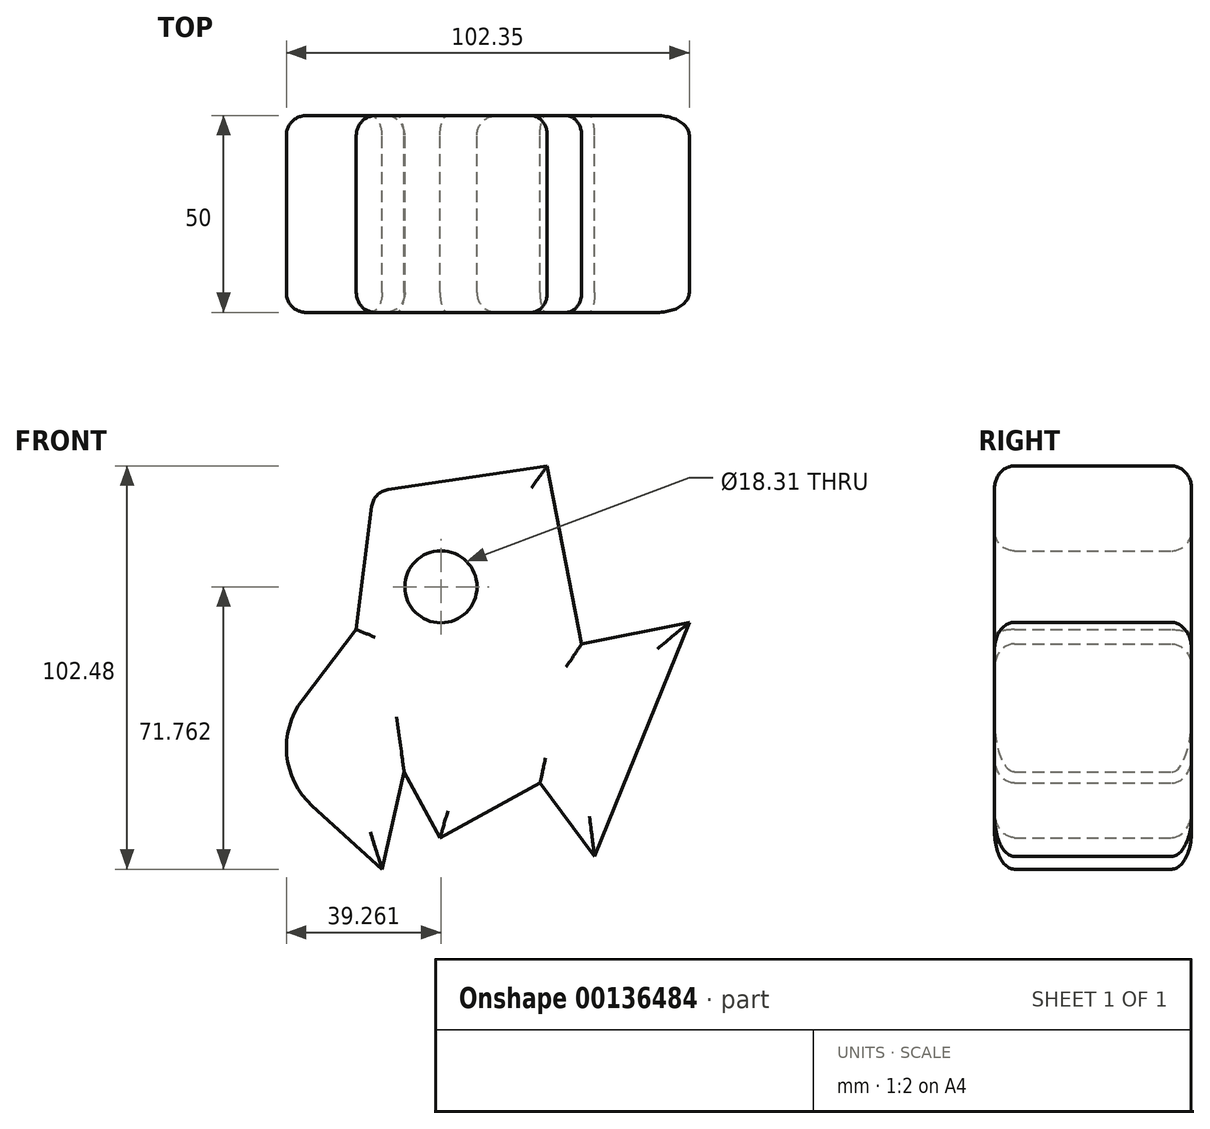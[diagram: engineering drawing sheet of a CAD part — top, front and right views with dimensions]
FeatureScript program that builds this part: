
annotation { "Feature Type Name" : "Feature", "Feature Type Description" : "" }
export const myFeature = defineFeature(function(context is Context, id is Id, definition is map)
    precondition{}
    {
        {
            var Q0;
            Q0=qCreatedBy(makeId("Front.planeOp"),FACE);
            var sketch = newSketch(context, id + "F0", { "sketchPlane" : qUnion([Q0])});
            skLineSegment(sketch, "E0", {"start": v(-30.63, 23.89) * mm, "end": v(-55.43, -8.57) * mm});
            skLineSegment(sketch, "E1", {"start": v(-55.43, -8.57) * mm, "end": v(-24.07, -37.02) * mm});
            skLineSegment(sketch, "E2", {"start": v(-9.35, -28.99) * mm, "end": v(16.05, -15.13) * mm});
            skLineSegment(sketch, "E3", {"start": v(16.05, -15.13) * mm, "end": v(29.9, -33.73) * mm});
            skLineSegment(sketch, "E4", {"start": v(29.9, -33.73) * mm, "end": v(53.97, 25.71) * mm});
            skLineSegment(sketch, "E5", {"start": v(53.97, 25.71) * mm, "end": v(26.62, 20.24) * mm});
            skLineSegment(sketch, "E6", {"start": v(26.62, 20.24) * mm, "end": v(17.87, 65.46) * mm});
            skLineSegment(sketch, "E7", {"start": v(17.87, 65.46) * mm, "end": v(-26.26, 58.9) * mm});
            skLineSegment(sketch, "E8", {"start": v(-26.26, 58.9) * mm, "end": v(-30.63, 23.89) * mm});
            skCircle(sketch, "E9", {"center": v(-9.12, 34.74) * mm, "radius": 9.16 * mm});
            skLineSegment(sketch, "E10", {"start": v(-18.47, -12.28) * mm, "end": v(-24.07, -37.02) * mm});
            skLineSegment(sketch, "E11", {"start": v(-18.47, -12.28) * mm, "end": v(-9.35, -28.99) * mm});
            skSolve(sketch);
        }
        {
            var Q0;
            Q0=makeQuery(id+"F0.imprint","IMPRINT",FACE,{"disambiguationData":[TD([[makeQuery(id+"F0.imprint","IMPRINT",EDGE,{"derivedFrom":sQuery(id+"F0.wireOp",EDGE,"E0")}),1.0]])]});
            extrude(context, id + "F1", {"entities" : qUnion([Q0]), "depth" : 50 * mm});
        }
        {
            var Q0;
            Q0=makeQuery(id+"F1.opExtrude","SWEPT_EDGE",EDGE,{"disambiguationData":[OSD([sQuery(id+"F0.wireOp",EDGE,"E0"),sQuery(id+"F0.wireOp",EDGE,"E1")])]});
            fillet(context, id + "F2", {"entities" : qUnion([Q0]), "radius" : 20 * mm, "tangentPropagation" : true, "allowEdgeOverflow" : false});
        }
        {
            var Q0;
            Q0=makeQuery(id+"F1.opExtrude","SWEPT_EDGE",EDGE,{"disambiguationData":[OSD([sQuery(id+"F0.wireOp",EDGE,"E7"),sQuery(id+"F0.wireOp",EDGE,"E8")])]});
            fillet(context, id + "F3", {"entities" : qUnion([Q0]), "radius" : 5 * mm, "tangentPropagation" : true, "allowEdgeOverflow" : false});
        }
        {
            var Q0;
            Q0=makeQuery(id+"F1.opExtrude","CAP_EDGE",EDGE,{"disambiguationData":[OSD([sQuery(id+"F0.wireOp",EDGE,"E0")])],"isStart":false});
            var Q1;
            {var subQ0=sQuery(id+"F0.wireOp",EDGE,"E1");var subQ1=sQuery(id+"F0.wireOp",EDGE,"E0");Q1=makeQuery(id+"F2.opFillet","BLEND_EDGE",EDGE,{"blendedFrom":[makeQuery(id+"F1.opExtrude","SWEPT_EDGE",EDGE,{"disambiguationData":[OSD([subQ1,subQ0])]}),makeQuery(id+"F1.opExtrude","CAP_FACE",FACE,{"disambiguationData":[OSD([subQ1,subQ0,sQuery(id+"F0.wireOp",EDGE,"E2"),sQuery(id+"F0.wireOp",EDGE,"E3"),sQuery(id+"F0.wireOp",EDGE,"E4"),sQuery(id+"F0.wireOp",EDGE,"E5"),sQuery(id+"F0.wireOp",EDGE,"E6"),sQuery(id+"F0.wireOp",EDGE,"E7"),sQuery(id+"F0.wireOp",EDGE,"E8"),sQuery(id+"F0.wireOp",EDGE,"E9"),sQuery(id+"F0.wireOp",EDGE,"E10"),sQuery(id+"F0.wireOp",EDGE,"E11")])],"isStart":false})],"blendedInto":[makeQuery(id+"F1.opExtrude","CAP_FACE",FACE,{"disambiguationData":[OSD([subQ1,subQ0,sQuery(id+"F0.wireOp",EDGE,"E2"),sQuery(id+"F0.wireOp",EDGE,"E3"),sQuery(id+"F0.wireOp",EDGE,"E4"),sQuery(id+"F0.wireOp",EDGE,"E5"),sQuery(id+"F0.wireOp",EDGE,"E6"),sQuery(id+"F0.wireOp",EDGE,"E7"),sQuery(id+"F0.wireOp",EDGE,"E8"),sQuery(id+"F0.wireOp",EDGE,"E9"),sQuery(id+"F0.wireOp",EDGE,"E10"),sQuery(id+"F0.wireOp",EDGE,"E11")])],"isStart":false})]});}
            var Q2;
            Q2=makeQuery(id+"F1.opExtrude","CAP_EDGE",EDGE,{"disambiguationData":[OSD([sQuery(id+"F0.wireOp",EDGE,"E7")])],"isStart":false});
            var Q3;
            Q3=makeQuery(id+"F1.opExtrude","CAP_EDGE",EDGE,{"disambiguationData":[OSD([sQuery(id+"F0.wireOp",EDGE,"E6")])],"isStart":false});
            var Q4;
            Q4=makeQuery(id+"F1.opExtrude","CAP_EDGE",EDGE,{"disambiguationData":[OSD([sQuery(id+"F0.wireOp",EDGE,"E5")])],"isStart":false});
            var Q5;
            Q5=makeQuery(id+"F1.opExtrude","CAP_FACE",FACE,{"disambiguationData":[OSD([sQuery(id+"F0.wireOp",EDGE,"E0"),sQuery(id+"F0.wireOp",EDGE,"E1"),sQuery(id+"F0.wireOp",EDGE,"E2"),sQuery(id+"F0.wireOp",EDGE,"E3"),sQuery(id+"F0.wireOp",EDGE,"E4"),sQuery(id+"F0.wireOp",EDGE,"E5"),sQuery(id+"F0.wireOp",EDGE,"E6"),sQuery(id+"F0.wireOp",EDGE,"E7"),sQuery(id+"F0.wireOp",EDGE,"E8"),sQuery(id+"F0.wireOp",EDGE,"E9"),sQuery(id+"F0.wireOp",EDGE,"E10"),sQuery(id+"F0.wireOp",EDGE,"E11")])],"isStart":false});
            var Q6;
            Q6=makeQuery(id+"F1.opExtrude","CAP_EDGE",EDGE,{"disambiguationData":[OSD([sQuery(id+"F0.wireOp",EDGE,"E10")])],"isStart":false});
            var Q7;
            Q7=makeQuery(id+"F1.opExtrude","CAP_EDGE",EDGE,{"disambiguationData":[OSD([sQuery(id+"F0.wireOp",EDGE,"E1")])],"isStart":false});
            var Q8;
            Q8=makeQuery(id+"F1.opExtrude","CAP_EDGE",EDGE,{"disambiguationData":[OSD([sQuery(id+"F0.wireOp",EDGE,"E11")])],"isStart":false});
            var Q9;
            Q9=makeQuery(id+"F1.opExtrude","CAP_EDGE",EDGE,{"disambiguationData":[OSD([sQuery(id+"F0.wireOp",EDGE,"E2")])],"isStart":false});
            var Q10;
            Q10=makeQuery(id+"F1.opExtrude","CAP_EDGE",EDGE,{"disambiguationData":[OSD([sQuery(id+"F0.wireOp",EDGE,"E3")])],"isStart":false});
            var Q11;
            {var subQ0=sQuery(id+"F0.wireOp",EDGE,"E8");var subQ1=sQuery(id+"F0.wireOp",EDGE,"E7");Q11=makeQuery(id+"F3.opFillet","BLEND_EDGE",EDGE,{"blendedFrom":[makeQuery(id+"F1.opExtrude","SWEPT_EDGE",EDGE,{"disambiguationData":[OSD([subQ1,subQ0])]}),makeQuery(id+"F1.opExtrude","CAP_FACE",FACE,{"disambiguationData":[OSD([sQuery(id+"F0.wireOp",EDGE,"E0"),sQuery(id+"F0.wireOp",EDGE,"E1"),sQuery(id+"F0.wireOp",EDGE,"E2"),sQuery(id+"F0.wireOp",EDGE,"E3"),sQuery(id+"F0.wireOp",EDGE,"E4"),sQuery(id+"F0.wireOp",EDGE,"E5"),sQuery(id+"F0.wireOp",EDGE,"E6"),subQ1,subQ0,sQuery(id+"F0.wireOp",EDGE,"E9"),sQuery(id+"F0.wireOp",EDGE,"E10"),sQuery(id+"F0.wireOp",EDGE,"E11")])],"isStart":false})],"blendedInto":[makeQuery(id+"F1.opExtrude","CAP_FACE",FACE,{"disambiguationData":[OSD([sQuery(id+"F0.wireOp",EDGE,"E0"),sQuery(id+"F0.wireOp",EDGE,"E1"),sQuery(id+"F0.wireOp",EDGE,"E2"),sQuery(id+"F0.wireOp",EDGE,"E3"),sQuery(id+"F0.wireOp",EDGE,"E4"),sQuery(id+"F0.wireOp",EDGE,"E5"),sQuery(id+"F0.wireOp",EDGE,"E6"),subQ1,subQ0,sQuery(id+"F0.wireOp",EDGE,"E9"),sQuery(id+"F0.wireOp",EDGE,"E10"),sQuery(id+"F0.wireOp",EDGE,"E11")])],"isStart":false})]});}
            var Q12;
            Q12=makeQuery(id+"F1.opExtrude","CAP_EDGE",EDGE,{"disambiguationData":[OSD([sQuery(id+"F0.wireOp",EDGE,"E8")])],"isStart":false});
            fillet(context, id + "F4", {"entities" : qUnion([Q0, Q1, Q2, Q3, Q4, Q5, Q6, Q7, Q8, Q9, Q10, Q11, Q12]), "radius" : 5 * mm, "tangentPropagation" : true, "allowEdgeOverflow" : false});
        }
        {
            var Q0;
            Q0=makeQuery(id+"F1.opExtrude","CAP_EDGE",EDGE,{"disambiguationData":[OSD([sQuery(id+"F0.wireOp",EDGE,"E6")])],"isStart":true});
            var Q1;
            Q1=makeQuery(id+"F1.opExtrude","CAP_EDGE",EDGE,{"disambiguationData":[OSD([sQuery(id+"F0.wireOp",EDGE,"E7")])],"isStart":true});
            var Q2;
            {var subQ0=sQuery(id+"F0.wireOp",EDGE,"E8");var subQ1=sQuery(id+"F0.wireOp",EDGE,"E7");Q2=makeQuery(id+"F3.opFillet","BLEND_EDGE",EDGE,{"blendedFrom":[makeQuery(id+"F1.opExtrude","SWEPT_EDGE",EDGE,{"disambiguationData":[OSD([subQ1,subQ0])]}),makeQuery(id+"F1.opExtrude","CAP_FACE",FACE,{"disambiguationData":[OSD([sQuery(id+"F0.wireOp",EDGE,"E0"),sQuery(id+"F0.wireOp",EDGE,"E1"),sQuery(id+"F0.wireOp",EDGE,"E2"),sQuery(id+"F0.wireOp",EDGE,"E3"),sQuery(id+"F0.wireOp",EDGE,"E4"),sQuery(id+"F0.wireOp",EDGE,"E5"),sQuery(id+"F0.wireOp",EDGE,"E6"),subQ1,subQ0,sQuery(id+"F0.wireOp",EDGE,"E9"),sQuery(id+"F0.wireOp",EDGE,"E10"),sQuery(id+"F0.wireOp",EDGE,"E11")])],"isStart":true})],"blendedInto":[makeQuery(id+"F1.opExtrude","CAP_FACE",FACE,{"disambiguationData":[OSD([sQuery(id+"F0.wireOp",EDGE,"E0"),sQuery(id+"F0.wireOp",EDGE,"E1"),sQuery(id+"F0.wireOp",EDGE,"E2"),sQuery(id+"F0.wireOp",EDGE,"E3"),sQuery(id+"F0.wireOp",EDGE,"E4"),sQuery(id+"F0.wireOp",EDGE,"E5"),sQuery(id+"F0.wireOp",EDGE,"E6"),subQ1,subQ0,sQuery(id+"F0.wireOp",EDGE,"E9"),sQuery(id+"F0.wireOp",EDGE,"E10"),sQuery(id+"F0.wireOp",EDGE,"E11")])],"isStart":true})]});}
            var Q3;
            Q3=makeQuery(id+"F1.opExtrude","CAP_EDGE",EDGE,{"disambiguationData":[OSD([sQuery(id+"F0.wireOp",EDGE,"E8")])],"isStart":true});
            var Q4;
            Q4=makeQuery(id+"F1.opExtrude","CAP_EDGE",EDGE,{"disambiguationData":[OSD([sQuery(id+"F0.wireOp",EDGE,"E0")])],"isStart":true});
            var Q5;
            {var subQ0=sQuery(id+"F0.wireOp",EDGE,"E1");var subQ1=sQuery(id+"F0.wireOp",EDGE,"E0");Q5=makeQuery(id+"F2.opFillet","BLEND_EDGE",EDGE,{"blendedFrom":[makeQuery(id+"F1.opExtrude","SWEPT_EDGE",EDGE,{"disambiguationData":[OSD([subQ1,subQ0])]}),makeQuery(id+"F1.opExtrude","CAP_FACE",FACE,{"disambiguationData":[OSD([subQ1,subQ0,sQuery(id+"F0.wireOp",EDGE,"E2"),sQuery(id+"F0.wireOp",EDGE,"E3"),sQuery(id+"F0.wireOp",EDGE,"E4"),sQuery(id+"F0.wireOp",EDGE,"E5"),sQuery(id+"F0.wireOp",EDGE,"E6"),sQuery(id+"F0.wireOp",EDGE,"E7"),sQuery(id+"F0.wireOp",EDGE,"E8"),sQuery(id+"F0.wireOp",EDGE,"E9"),sQuery(id+"F0.wireOp",EDGE,"E10"),sQuery(id+"F0.wireOp",EDGE,"E11")])],"isStart":true})],"blendedInto":[makeQuery(id+"F1.opExtrude","CAP_FACE",FACE,{"disambiguationData":[OSD([subQ1,subQ0,sQuery(id+"F0.wireOp",EDGE,"E2"),sQuery(id+"F0.wireOp",EDGE,"E3"),sQuery(id+"F0.wireOp",EDGE,"E4"),sQuery(id+"F0.wireOp",EDGE,"E5"),sQuery(id+"F0.wireOp",EDGE,"E6"),sQuery(id+"F0.wireOp",EDGE,"E7"),sQuery(id+"F0.wireOp",EDGE,"E8"),sQuery(id+"F0.wireOp",EDGE,"E9"),sQuery(id+"F0.wireOp",EDGE,"E10"),sQuery(id+"F0.wireOp",EDGE,"E11")])],"isStart":true})]});}
            var Q6;
            Q6=makeQuery(id+"F1.opExtrude","CAP_FACE",FACE,{"disambiguationData":[OSD([sQuery(id+"F0.wireOp",EDGE,"E0"),sQuery(id+"F0.wireOp",EDGE,"E1"),sQuery(id+"F0.wireOp",EDGE,"E2"),sQuery(id+"F0.wireOp",EDGE,"E3"),sQuery(id+"F0.wireOp",EDGE,"E4"),sQuery(id+"F0.wireOp",EDGE,"E5"),sQuery(id+"F0.wireOp",EDGE,"E6"),sQuery(id+"F0.wireOp",EDGE,"E7"),sQuery(id+"F0.wireOp",EDGE,"E8"),sQuery(id+"F0.wireOp",EDGE,"E9"),sQuery(id+"F0.wireOp",EDGE,"E10"),sQuery(id+"F0.wireOp",EDGE,"E11")])],"isStart":true});
            var Q7;
            Q7=makeQuery(id+"F1.opExtrude","CAP_EDGE",EDGE,{"disambiguationData":[OSD([sQuery(id+"F0.wireOp",EDGE,"E1")])],"isStart":true});
            var Q8;
            Q8=makeQuery(id+"F1.opExtrude","CAP_EDGE",EDGE,{"disambiguationData":[OSD([sQuery(id+"F0.wireOp",EDGE,"E10")])],"isStart":true});
            var Q9;
            Q9=makeQuery(id+"F1.opExtrude","CAP_EDGE",EDGE,{"disambiguationData":[OSD([sQuery(id+"F0.wireOp",EDGE,"E2")])],"isStart":true});
            var Q10;
            Q10=makeQuery(id+"F1.opExtrude","CAP_EDGE",EDGE,{"disambiguationData":[OSD([sQuery(id+"F0.wireOp",EDGE,"E3")])],"isStart":true});
            var Q11;
            Q11=makeQuery(id+"F1.opExtrude","CAP_EDGE",EDGE,{"disambiguationData":[OSD([sQuery(id+"F0.wireOp",EDGE,"E5")])],"isStart":true});
            var Q12;
            Q12=makeQuery(id+"F1.opExtrude","CAP_EDGE",EDGE,{"disambiguationData":[OSD([sQuery(id+"F0.wireOp",EDGE,"E9")])],"isStart":true});
            var Q13;
            Q13=makeQuery(id+"F1.opExtrude","CAP_EDGE",EDGE,{"disambiguationData":[OSD([sQuery(id+"F0.wireOp",EDGE,"E11")])],"isStart":true});
            fillet(context, id + "F5", {"entities" : qUnion([Q0, Q1, Q2, Q3, Q4, Q5, Q6, Q7, Q8, Q9, Q10, Q11, Q12, Q13]), "radius" : 5 * mm, "tangentPropagation" : true, "allowEdgeOverflow" : false});
        }
    });
